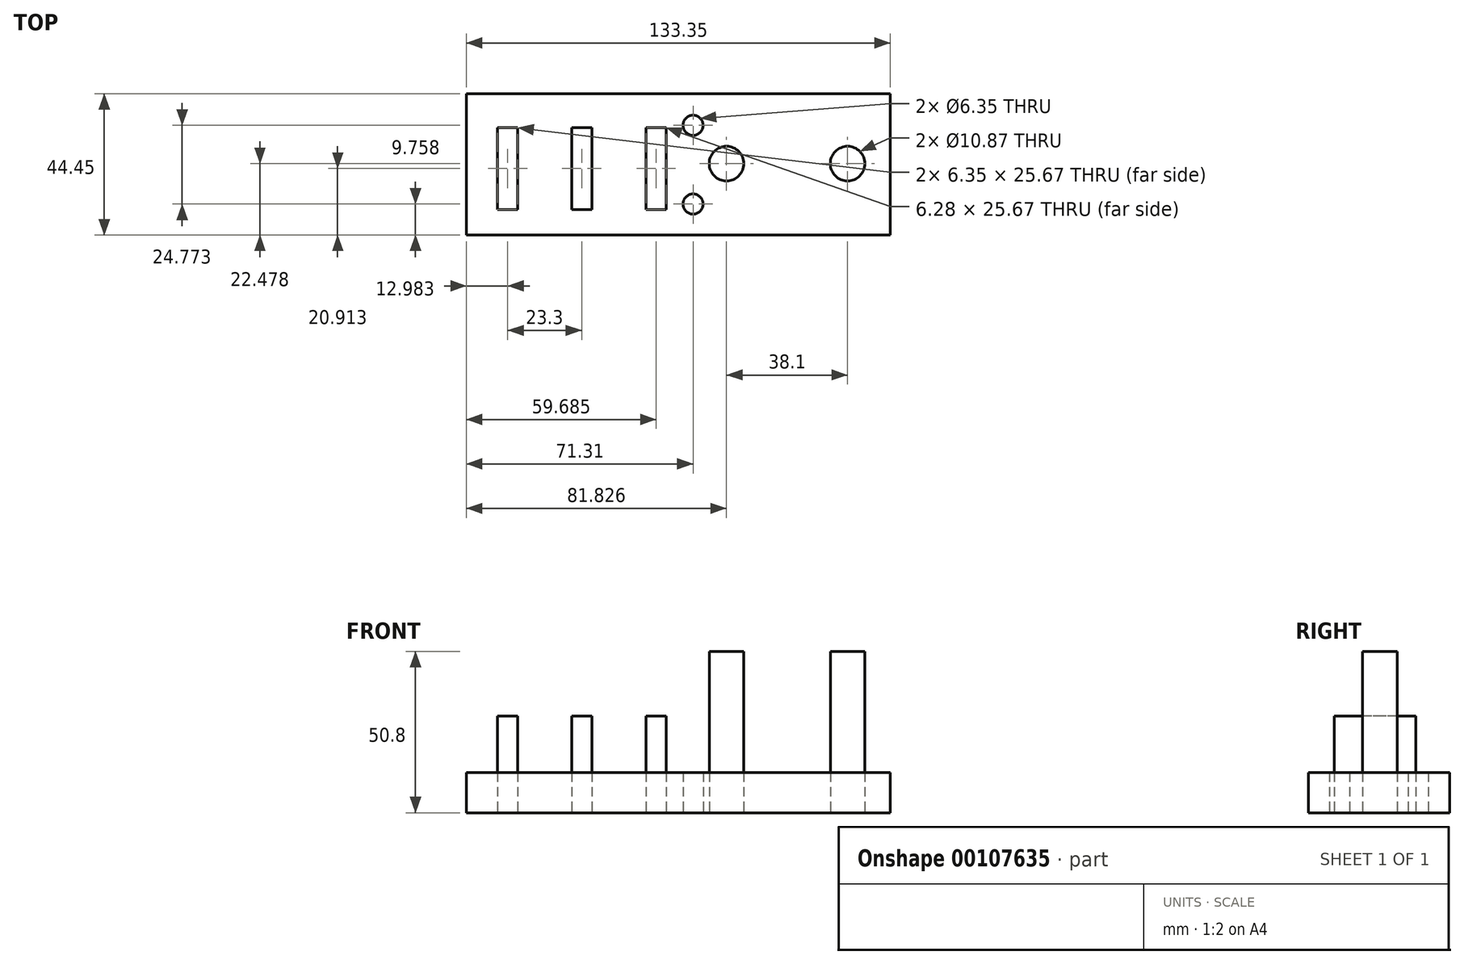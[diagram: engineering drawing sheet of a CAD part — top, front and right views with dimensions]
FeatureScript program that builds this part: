
annotation { "Feature Type Name" : "Feature", "Feature Type Description" : "" }
export const myFeature = defineFeature(function(context is Context, id is Id, definition is map)
    precondition{}
    {
        {
            var Q0;
            Q0=qCreatedBy(makeId("Top.planeOp"),FACE);
            var sketch = newSketch(context, id + "F0", { "sketchPlane" : qUnion([Q0])});
            skLineSegment(sketch, "E0", {"start": v(-80.02, -14.32) * mm, "end": v(-80.02, 30.13) * mm});
            skLineSegment(sketch, "E1", {"start": v(53.33, 30.13) * mm, "end": v(53.33, -14.32) * mm});
            skLineSegment(sketch, "E2", {"start": v(53.33, -14.32) * mm, "end": v(-80.02, -14.32) * mm});
            skLineSegment(sketch, "E3", {"start": v(-80.02, 30.13) * mm, "end": v(53.33, 30.13) * mm});
            skLineSegment(sketch, "E4", {"start": v(-70.21, -6.24) * mm, "end": v(-63.86, -6.24) * mm});
            skLineSegment(sketch, "E5", {"start": v(-70.21, 19.43) * mm, "end": v(-63.86, 19.43) * mm});
            skLineSegment(sketch, "E6", {"start": v(-46.84, 19.43) * mm, "end": v(-40.5, 19.43) * mm});
            skLineSegment(sketch, "E7", {"start": v(-40.5, -6.24) * mm, "end": v(-46.84, -6.24) * mm});
            skLineSegment(sketch, "E8", {"start": v(-70.21, 19.43) * mm, "end": v(-70.21, -6.24) * mm});
            skLineSegment(sketch, "E9", {"start": v(-63.86, 19.43) * mm, "end": v(-63.86, -6.24) * mm});
            skLineSegment(sketch, "E10", {"start": v(-63.86, 6.6) * mm, "end": v(-46.84, 6.6) * mm, "construction": true});
            skLineSegment(sketch, "E11.MirrorCS", {"start": v(-46.91, 19.43) * mm, "end": v(-46.91, -6.24) * mm});
            skLineSegment(sketch, "E12.MirrorCS", {"start": v(-40.56, 19.43) * mm, "end": v(-46.91, 19.43) * mm});
            skLineSegment(sketch, "E13.MirrorCS", {"start": v(-40.56, 19.43) * mm, "end": v(-40.56, -6.24) * mm});
            skLineSegment(sketch, "E14.MirrorCS", {"start": v(-46.91, -6.24) * mm, "end": v(-40.56, -6.24) * mm});
            skLineSegment(sketch, "E15.MirrorCS", {"start": v(-23.48, 19.43) * mm, "end": v(-23.48, -6.24) * mm});
            skLineSegment(sketch, "E16.MirrorCS", {"start": v(-17.2, 19.43) * mm, "end": v(-23.54, 19.43) * mm});
            skLineSegment(sketch, "E17.MirrorCS", {"start": v(-17.2, 19.43) * mm, "end": v(-17.2, -6.24) * mm});
            skLineSegment(sketch, "E18.MirrorCS", {"start": v(-17.2, -6.24) * mm, "end": v(-23.54, -6.24) * mm});
            skCircle(sketch, "E19", {"center": v(1.8, 8.16) * mm, "radius": 5.44 * mm});
            skCircle(sketch, "E20", {"center": v(39.9, 8.16) * mm, "radius": 5.44 * mm});
            skCircle(sketch, "E21", {"center": v(-8.71, 20.21) * mm, "radius": 3.18 * mm});
            skCircle(sketch, "E22", {"center": v(-8.71, -4.56) * mm, "radius": 3.18 * mm});
            skLineSegment(sketch, "E23", {"start": v(53.33, 7.9) * mm, "end": v(45.34, 7.9) * mm, "construction": true});
            skLineSegment(sketch, "E24", {"start": v(-40.5, 6.6) * mm, "end": v(-23.48, 6.6) * mm, "construction": true});
            skSolve(sketch);
        }
        {
            var Q0;
            Q0=makeQuery(id+"F0.imprint","IMPRINT",FACE,{"disambiguationData":[TD([[makeQuery(id+"F0.imprint","IMPRINT",EDGE,{"derivedFrom":sQuery(id+"F0.wireOp",EDGE,"E4")}),1.0]])]});
            var Q1;
            Q1=makeQuery(id+"F0.imprint","IMPRINT",FACE,{"disambiguationData":[TD([[makeQuery(id+"F0.imprint","IMPRINT",EDGE,{"derivedFrom":sQuery(id+"F0.wireOp",EDGE,"E6")}),-1.0]])]});
            var Q2;
            Q2=makeQuery(id+"F0.imprint","IMPRINT",FACE,{"disambiguationData":[TD([[makeQuery(id+"F0.imprint","IMPRINT",EDGE,{"derivedFrom":sQuery(id+"F0.wireOp",EDGE,"E11.MirrorCS")}),1.0]])]});
            var Q3;
            Q3=makeQuery(id+"F0.imprint","IMPRINT",FACE,{"disambiguationData":[TD([[makeQuery(id+"F0.imprint","IMPRINT",EDGE,{"derivedFrom":sQuery(id+"F0.wireOp",EDGE,"E15.MirrorCS")}),1.0]])]});
            extrude(context, id + "F1", {"entities" : qUnion([Q0, Q1, Q2, Q3]), "depth" : 30.48 * mm});
        }
        {
            var Q0;
            Q0=makeQuery(id+"F0.imprint","IMPRINT",FACE,{"disambiguationData":[TD([[makeQuery(id+"F0.imprint","IMPRINT",EDGE,{"derivedFrom":sQuery(id+"F0.wireOp",EDGE,"E19")}),1.0]])]});
            var Q1;
            Q1=makeQuery(id+"F0.imprint","IMPRINT",FACE,{"disambiguationData":[TD([[makeQuery(id+"F0.imprint","IMPRINT",EDGE,{"derivedFrom":sQuery(id+"F0.wireOp",EDGE,"E20")}),1.0]])]});
            extrude(context, id + "F2", {"entities" : qUnion([Q0, Q1]), "operationType" : NewBodyOperationType.ADD, "depth" : 50.8 * mm});
        }
        {
            var Q0;
            Q0=makeQuery(id+"F0.imprint","IMPRINT",FACE,{"disambiguationData":[TD([[makeQuery(id+"F0.imprint","IMPRINT",EDGE,{"derivedFrom":sQuery(id+"F0.wireOp",EDGE,"E0")}),-1.0]])]});
            extrude(context, id + "F3", {"entities" : qUnion([Q0]), "depth" : 12.7 * mm});
        }
    });
